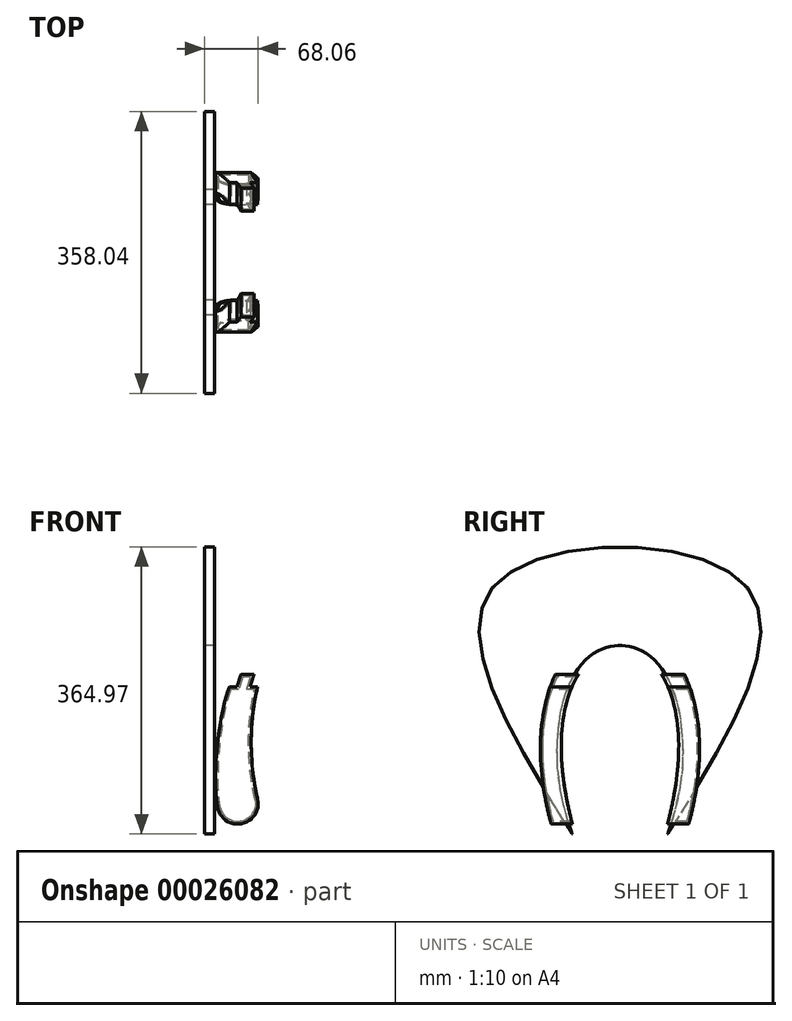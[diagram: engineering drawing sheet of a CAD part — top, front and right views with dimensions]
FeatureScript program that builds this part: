
annotation { "Feature Type Name" : "Feature", "Feature Type Description" : "" }
export const myFeature = defineFeature(function(context is Context, id is Id, definition is map)
    precondition{}
    {
        {
            var Q0;
            Q0=qCreatedBy(makeId("Front.planeOp"),FACE);
            var sketch = newSketch(context, id + "F0", { "sketchPlane" : qUnion([Q0])});
            skFitSpline(sketch, "E0", {"points": [v(31.64, 77.58) * mm, v(17.17, -78.03) * mm], "startDerivative": vector(-55.68, -149.28) * mm, "endDerivative": vector(17.93, -63.48) * mm});
            skFitSpline(sketch, "E1", {"points": [v(67.48, 77.58) * mm, v(67.38, -65.05) * mm], "startDerivative": vector(-39.1, -158.75) * mm, "endDerivative": vector(25.77, -109.76) * mm});
            skLineSegment(sketch, "E2", {"start": v(31.64, 77.58) * mm, "end": v(41.16, 77.58) * mm});
            skLineSegment(sketch, "E3", {"start": v(41.16, 77.58) * mm, "end": v(46.19, 93.44) * mm});
            skLineSegment(sketch, "E4", {"start": v(46.19, 93.44) * mm, "end": v(63, 93.44) * mm});
            skLineSegment(sketch, "E5", {"start": v(63, 93.44) * mm, "end": v(57.96, 77.58) * mm});
            skLineSegment(sketch, "E6", {"start": v(57.96, 77.58) * mm, "end": v(67.48, 77.58) * mm});
            skArc(sketch, "E7", {"start": v(17.17, -78.03) * mm, "mid": v(48.62, -96.09) * mm, "end": v(67.38, -65.05) * mm});
            skLineSegment(sketch, "E8", {"start": v(-140.74, 134.35) * mm, "end": v(-140.74, -43.45) * mm, "construction": true});
            skSolve(sketch);
        }
        {
            var Q0;
            Q0 = qSketchRegion(id + "F0", true);
            extrude(context, id + "F1", {"entities" : qUnion([Q0]), "oppositeDirection" : true, "depth" : 203.2 * mm});
        }
        {
            var Q0;
            Q0=qCreatedBy(makeId("Right.planeOp"),FACE);
            var sketch = newSketch(context, id + "F2", { "sketchPlane" : qUnion([Q0])});
            skFitSpline(sketch, "E9", {"points": [v(48.19, -121.04) * mm, v(155.01, -121.04) * mm], "startDerivative": vector(-310.01, 990.6) * mm, "endDerivative": vector(-310.01, -990.6) * mm});
            skLineSegment(sketch, "E10", {"start": v(-55.15, 209.16) * mm, "end": v(-55.15, -121.04) * mm});
            skLineSegment(sketch, "E11", {"start": v(-55.15, -121.04) * mm, "end": v(48.19, -121.04) * mm});
            skLineSegment(sketch, "E12", {"start": v(155.01, -121.04) * mm, "end": v(258.35, -121.04) * mm});
            skLineSegment(sketch, "E13", {"start": v(258.35, -121.04) * mm, "end": v(258.35, 209.16) * mm});
            skLineSegment(sketch, "E14", {"start": v(48.19, -121.04) * mm, "end": v(155.01, -121.04) * mm});
            skLineSegment(sketch, "E15", {"start": v(101.6, -121.04) * mm, "end": v(101.6, 126.6) * mm, "construction": true});
            skLineSegment(sketch, "E16.0", {"start": v(203.2, -65.05) * mm, "end": v(0, -65.05) * mm, "construction": true});
            skPoint(sketch, "E17", {"position": v(101.6, 2.78) * mm});
            skLineSegment(sketch, "E18", {"start": v(26.99, 2.78) * mm, "end": v(176.21, 2.78) * mm, "construction": true});
            skFitSpline(sketch, "E19.0", {"points": [v(23.95, -128.63) * mm, v(17.21, -107.12) * mm, v(7.06, -66.51) * mm, v(0.67, -12.76) * mm, v(1.88, 26.15) * mm, v(6.35, 53.78) * mm, v(11.37, 72.75) * mm, v(17.96, 89.95) * mm, v(26.08, 105.35) * mm, v(35.66, 118.87) * mm, v(46.65, 130.4) * mm, v(58.95, 139.76) * mm, v(72.41, 146.72) * mm, v(86.76, 151.03) * mm, v(101.6, 152.5) * mm, v(116.44, 151.03) * mm, v(130.79, 146.72) * mm, v(144.25, 139.76) * mm, v(156.55, 130.4) * mm, v(167.54, 118.87) * mm, v(177.12, 105.35) * mm, v(185.24, 89.95) * mm, v(191.83, 72.75) * mm, v(196.85, 53.78) * mm, v(201.32, 26.15) * mm, v(202.53, -12.76) * mm, v(196.14, -66.51) * mm, v(185.99, -107.12) * mm, v(179.25, -128.63) * mm]});
            skLineSegment(sketch, "E20", {"start": v(-55.15, 209.16) * mm, "end": v(258.35, 209.16) * mm});
            skPoint(sketch, "E21", {"position": v(101.6, -65.05) * mm});
            skSolve(sketch);
        }
        {
            var Q0;
            {var subQ6=sQuery(id+"F2.wireOp",EDGE,"E10");Q0=makeQuery(id+"F2.imprint","IMPRINT",FACE,{"disambiguationData":[TD([[makeQuery(id+"F2.imprint","IMPRINT",EDGE,{"derivedFrom":subQ6}),1.0]])]});}
            var Q1;
            Q1=makeQuery(id+"F2.imprint","IMPRINT",FACE,{"disambiguationData":[TD([[makeQuery(id+"F2.imprint","IMPRINT",EDGE,{"derivedFrom":sQuery(id+"F2.wireOp",EDGE,"E9")}),-1.0]])]});
            extrude(context, id + "F3", {"entities" : qUnion([Q0, Q1]), "operationType" : NewBodyOperationType.REMOVE, "endBound" : BoundingType.THROUGH_ALL, "depth" : 76.2 * mm});
        }
        {
            var Q0;
            Q0=makeQuery(id+"F3.boolean.opBoolean","COPY",FACE,{"disambiguationData":[OD(1.0)],"derivedFrom":makeQuery(id+"F3.opExtrude","SWEPT_FACE",FACE,{"disambiguationData":[OSD([sQuery(id+"F2.wireOp",EDGE,"E9")])]})});
            var Q1;
            Q1=makeQuery(id+"F3.boolean.opBoolean","COPY",FACE,{"disambiguationData":[OD(0.0)],"derivedFrom":makeQuery(id+"F3.opExtrude","SWEPT_FACE",FACE,{"disambiguationData":[OSD([sQuery(id+"F2.wireOp",EDGE,"E9")])]})});
            shell(context, id + "F4", {"entities" : qUnion([Q0, Q1]), "thickness" : 3.17 * mm});
        }
        {
            var Q0;
            Q0=qCreatedBy(makeId("Right.planeOp"),FACE);
            var sketch = newSketch(context, id + "F5", { "sketchPlane" : qUnion([Q0])});
            skFitSpline(sketch, "E22.0", {"points": [v(48.19, -121.04) * mm, v(-55.15, 209.16) * mm, v(258.35, 209.16) * mm, v(155.01, -121.04) * mm]});
            skFitSpline(sketch, "E23.0", {"points": [v(45.16, -122) * mm, v(32.17, -80.5) * mm, v(22.48, -25.94) * mm, v(24.34, 31.5) * mm, v(31.95, 66.94) * mm, v(44.62, 94.72) * mm, v(61.24, 114.8) * mm, v(77.42, 125) * mm, v(91.13, 129.1) * mm, v(101.6, 130.13) * mm, v(112.07, 129.1) * mm, v(125.78, 125) * mm, v(141.96, 114.8) * mm, v(158.58, 94.72) * mm, v(171.25, 66.94) * mm, v(178.86, 31.5) * mm, v(180.72, -25.94) * mm, v(171.03, -80.5) * mm, v(158.04, -122) * mm]});
            skLineSegment(sketch, "E24.0", {"start": v(28.05, 25.25) * mm, "end": v(24.86, 25.25) * mm});
            skLineSegment(sketch, "E24.1", {"start": v(178.34, 25.25) * mm, "end": v(175.15, 25.25) * mm});
            skPoint(sketch, "E25.orphan", {"position": v(48.19, -121.04) * mm});
            skPoint(sketch, "E26.orphan", {"position": v(155.01, -121.04) * mm});
            skSolve(sketch);
        }
        {
            var Q0;
            Q0 = qSketchRegion(id + "F5", true);
            extrude(context, id + "F6", {"entities" : qUnion([Q0]), "depth" : 12.7 * mm});
        }
    });
